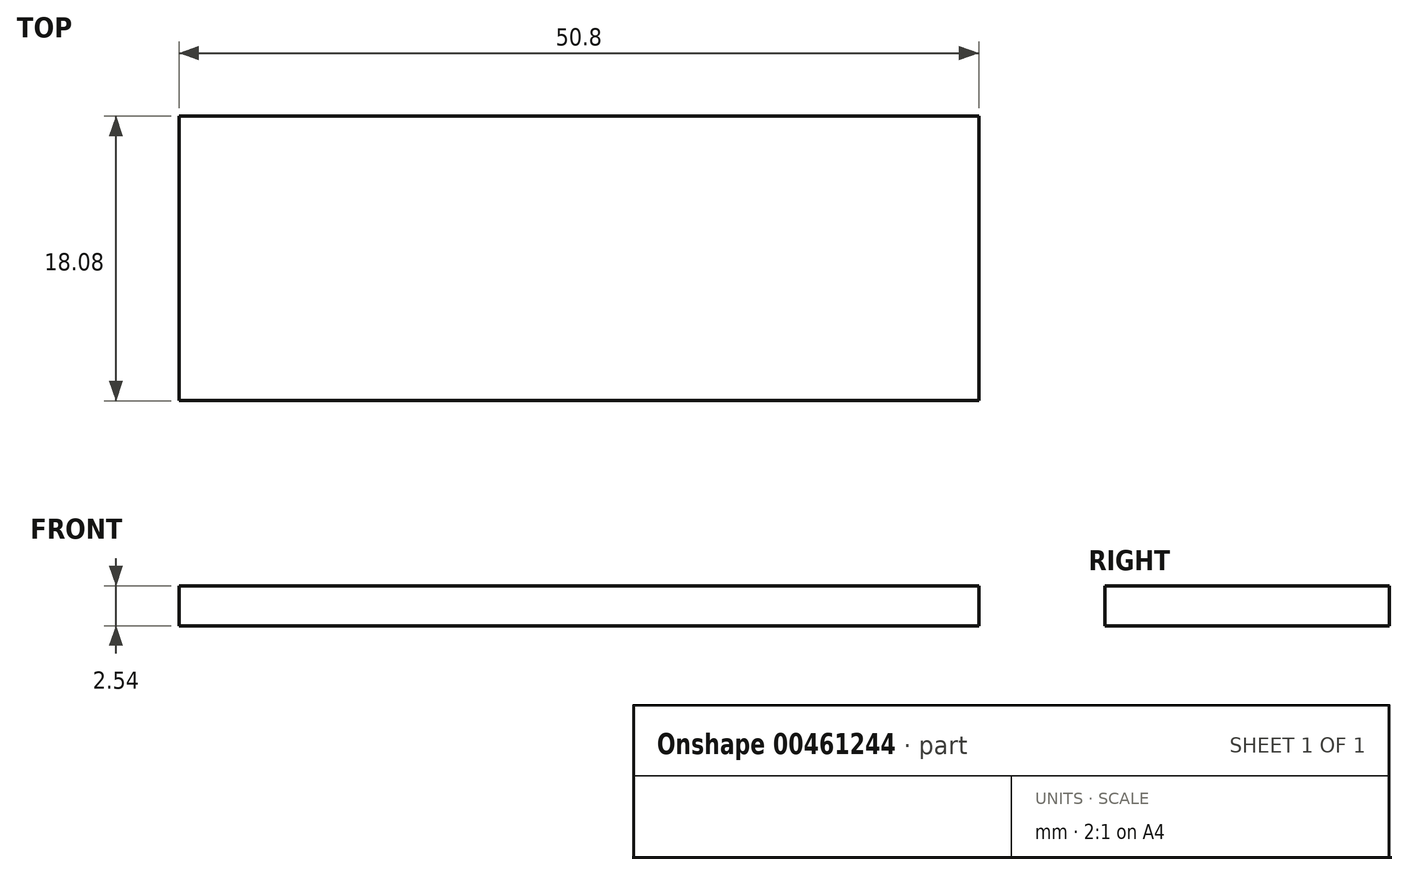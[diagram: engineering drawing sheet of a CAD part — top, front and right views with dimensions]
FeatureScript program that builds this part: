
annotation { "Feature Type Name" : "Feature", "Feature Type Description" : "" }
export const myFeature = defineFeature(function(context is Context, id is Id, definition is map)
    precondition{}
    {
        {
            var Q0;
            Q0=qCreatedBy(makeId("Top.planeOp"),FACE);
            var sketch = newSketch(context, id + "F0", { "sketchPlane" : qUnion([Q0])});
            skLineSegment(sketch, "E0", {"start": v(-11.7, 0.23) * mm, "end": v(39.1, 0.23) * mm});
            skLineSegment(sketch, "E1", {"start": v(-11.7, 0.23) * mm, "end": v(-11.7, -17.85) * mm});
            skLineSegment(sketch, "E2", {"start": v(-11.7, -17.85) * mm, "end": v(39.1, -17.85) * mm});
            skLineSegment(sketch, "E3", {"start": v(39.1, -17.85) * mm, "end": v(39.1, 0.23) * mm});
            skSolve(sketch);
        }
        {
            var Q0;
            Q0=qSketchRegion(id+"F0",true);
            extrude(context, id + "F1", {"entities" : qUnion([Q0]), "depth" : 2.54 * mm});
        }
    });
